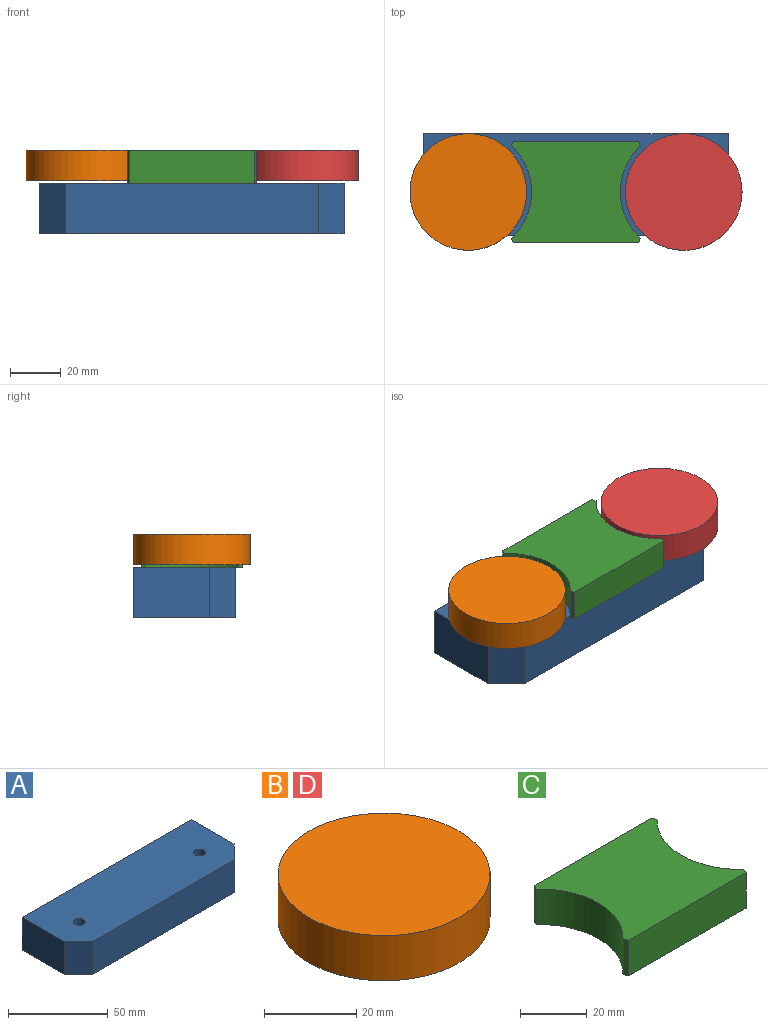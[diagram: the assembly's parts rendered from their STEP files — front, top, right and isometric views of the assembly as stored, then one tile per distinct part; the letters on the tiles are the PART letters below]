
ASSEMBLY  parts=4 mates=3
PART A: 10 faces, bbox 120x40x20 mm
  f0: plane 120x20mm, normal (0,1,0), area 2400mm2, adj f1,f6,f8,f9
  f1: plane 30x20mm, normal (-1,0,0), area 600mm2, adj f0,f2,f8,f9
  f2: plane 20x10mm, normal (-0.71,-0.71,0), area 282.8mm2, adj f1,f3,f8,f9
  f3: plane 100x20mm, normal (0,-1,0), area 2000mm2, adj f2,f4,f8,f9
  f4: plane 20x10mm, normal (0.71,-0.71,0), area 282.8mm2, adj f3,f6,f8,f9
  f5: cylinder r=3mm len=20mm, axis (0,0,-1), area 377mm2, adj f8,f9
  f6: plane 30x20mm, normal (1,0,0), area 600mm2, adj f0,f4,f8,f9
  f7: cylinder r=3mm len=20mm, axis (0,0,-1), area 377mm2, adj f8,f9
  f8: plane 120x40mm, normal (0,0,1), area 4643.5mm2, adj f0,f1,f2,f3,f4,f5,f6,f7
  f9: plane 120x40mm, normal (0,0,-1), area 4643.5mm2, adj f0,f1,f2,f3,f4,f5,f6,f7
PART B: 3 faces, bbox 46x46x12 mm
  f0: cylinder r=23mm len=46mm, axis (0,0,-1), area 1734.2mm2, adj f1,f2
  f1: plane 46x46mm, normal (0,0,1), area 1661.9mm2, adj f0
  f2: plane 46x46mm, normal (0,0,-1), area 1661.9mm2, adj f0
PART C: 10 faces, bbox 50.9x40x13 mm
  f0: plane 49.5x13mm, normal (0,1,0), area 643.5mm2, adj f4,f5,f8,f9
  f1: cylinder r=25mm len=36.54mm, axis (0,0,-1), area 532.6mm2, adj f4,f5,f6,f9
  f2: plane 49.5x13mm, normal (0,-1,0), area 643.5mm2, adj f4,f5,f6,f7
  f3: cylinder r=25mm len=36.54mm, axis (0,0,-1), area 532.6mm2, adj f4,f5,f7,f8
  f4: plane 50.87x40mm, normal (0,0,1), area 1631.6mm2, adj f0,f1,f2,f3,f6,f7,f8,f9
  f5: plane 50.87x40mm, normal (0,0,-1), area 1631.6mm2, adj f0,f1,f2,f3,f6,f7,f8,f9
  f6: plane 13x1.73mm, normal (-0.93,-0.37,0), area 24.2mm2, adj f1,f2,f4,f5
  f7: plane 13x1.73mm, normal (0.93,-0.37,0), area 24.2mm2, adj f2,f3,f4,f5
  f8: plane 13x1.73mm, normal (0.93,0.37,0), area 24.2mm2, adj f0,f3,f4,f5
  f9: plane 13x1.73mm, normal (-0.93,0.37,0), area 24.2mm2, adj f0,f1,f4,f5
PART D: same geometry as B
PLACE A t=(-7.66,27.8,-26.72)mm
PLACE B t=(9.84,4.8,-5.72)mm
PLACE C t=(9.84,4.8,-6.72)mm
PLACE D t=(94.84,4.8,-5.72)mm
MATE revolute B.f0 <-> A.f5  axis (0,0,-1) through (9.84,4.8,-5.72)mm
MATE fastened A.f7 <-> C.f3  axis (0,0,1) through (94.84,4.8,-6.72)mm
MATE revolute A.f7 <-> D.f0  axis (0,0,1) through (94.84,4.8,-6.72)mm
